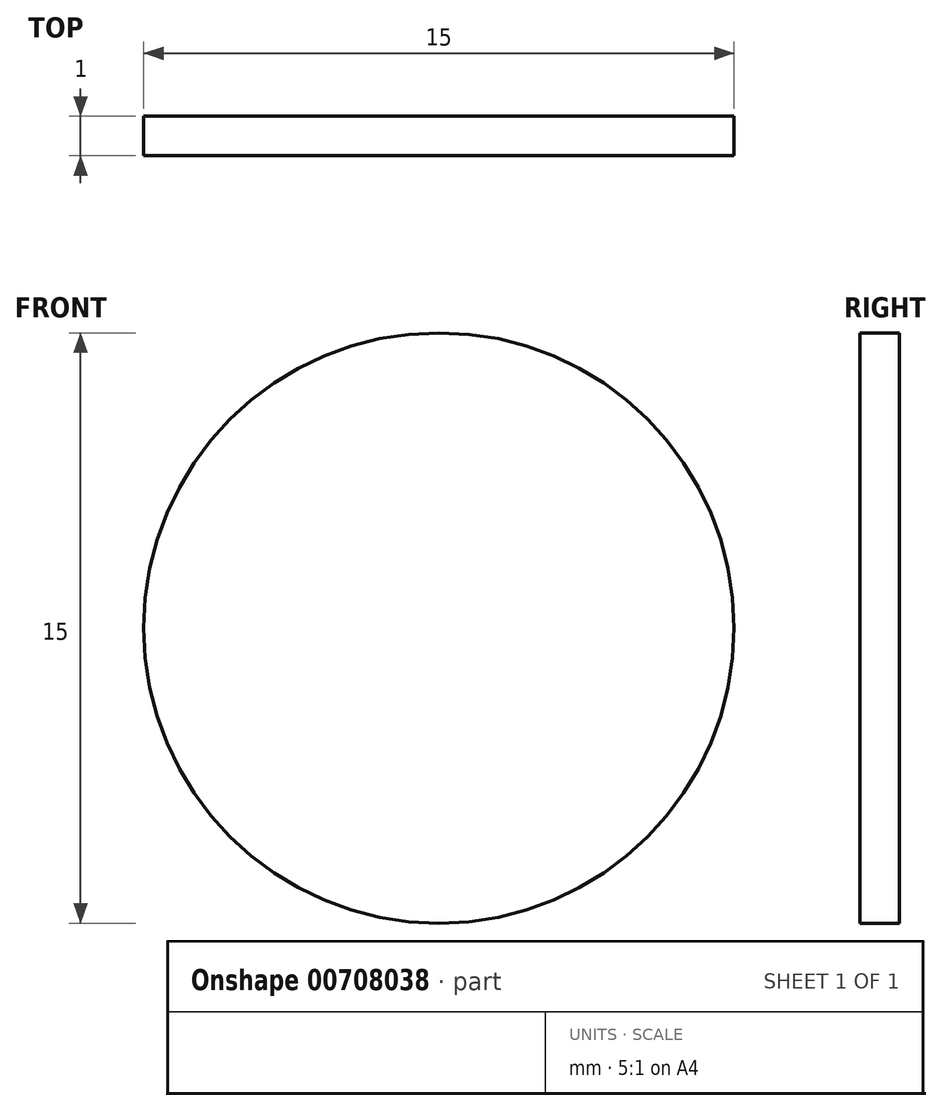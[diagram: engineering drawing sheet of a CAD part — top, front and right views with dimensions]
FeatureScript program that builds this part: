
annotation { "Feature Type Name" : "Feature", "Feature Type Description" : "" }
export const myFeature = defineFeature(function(context is Context, id is Id, definition is map)
    precondition{}
    {
        {
            var Q0;
            Q0=qCreatedBy(makeId("Front.planeOp"),FACE);
            var sketch = newSketch(context, id + "F0", { "sketchPlane" : qUnion([Q0])});
            skCircle(sketch, "E0", {"center": v(0, 0) * mm, "radius": 7.5 * mm});
            skSolve(sketch);
        }
        {
            var Q0;
            Q0=makeQuery(id+"F0.imprint","IMPRINT",FACE,{"disambiguationData":[TD([[makeQuery(id+"F0.imprint","IMPRINT",EDGE,{"derivedFrom":sQuery(id+"F0.wireOp",EDGE,"E0")}),1.0]])]});
            extrude(context, id + "F1", {"entities" : qUnion([Q0]), "depth" : 1 * mm, "offsetDistance" : 25 * mm});
        }
    });
